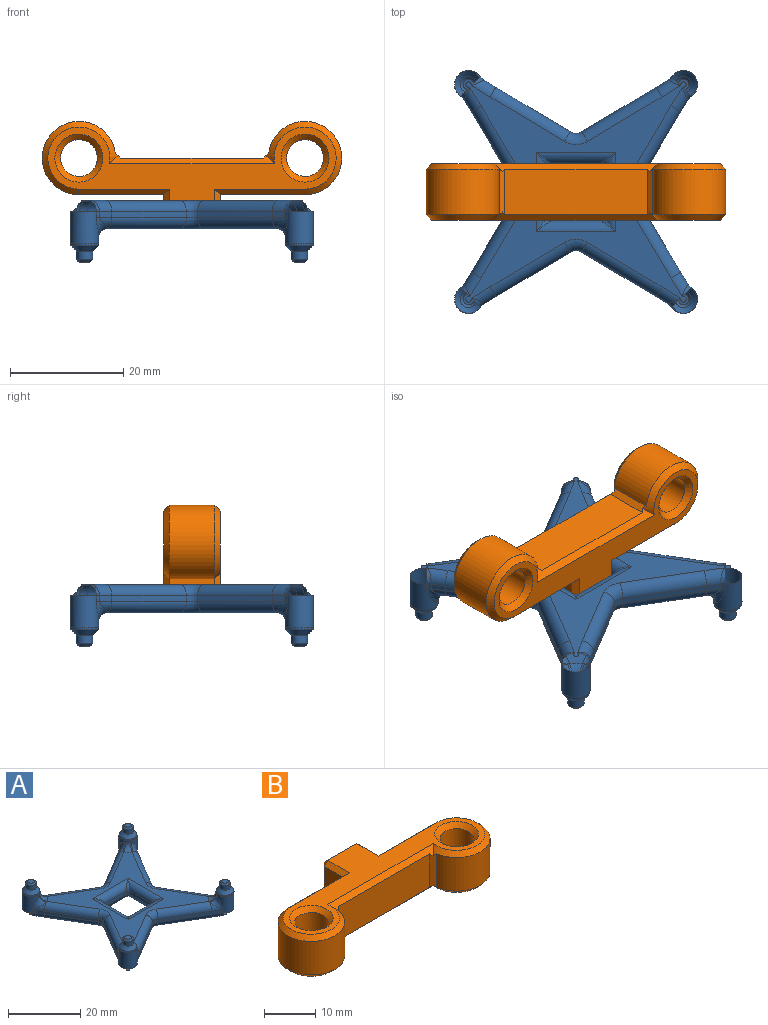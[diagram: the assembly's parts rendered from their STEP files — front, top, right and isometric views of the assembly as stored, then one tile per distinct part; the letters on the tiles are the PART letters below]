
ASSEMBLY  parts=2 mates=1
PART A: 150 faces, bbox 45x45x13 mm
  f0: plane 33.47x33.47mm, normal (0,0,1), area 377.1mm2, adj f40,f41,f42,f53,f54,f57,f58,f59
  f1: plane 41x41mm, normal (0,0,-1), area 402.7mm2, adj f44,f45,f46,f49,f50,f55,f56,f60
  f2: cylinder r=2.5mm len=5.56mm, axis (0,0,-1), area 58.7mm2, adj f73,f138,f139,f140,f142,f143,f144,f145
  f3: cylinder r=1.45mm len=2.9mm, axis (0,0,-1), area 13.7mm2, adj f17,f109
  f4: plane 1.9x1.9mm, normal (0,0,1), area 2.8mm2, adj f17
  f5: cylinder r=2.5mm len=5.56mm, axis (0,0,-1), area 58.7mm2, adj f74,f120,f121,f122,f123,f125,f126,f127
  f6: cylinder r=1.45mm len=2.9mm, axis (0,0,-1), area 13.7mm2, adj f16,f106
  f7: plane 1.9x1.9mm, normal (0,0,1), area 2.8mm2, adj f16
  f8: cylinder r=2.5mm len=5.56mm, axis (0,0,-1), area 58.7mm2, adj f56,f111,f112,f113,f115,f116,f117,f118
  f9: cylinder r=1.45mm len=2.9mm, axis (0,0,-1), area 13.7mm2, adj f15,f107
  f10: plane 1.9x1.9mm, normal (0,0,1), area 2.8mm2, adj f15
  f11: cylinder r=2.5mm len=5.56mm, axis (0,0,-1), area 58.7mm2, adj f55,f129,f130,f131,f133,f134,f135,f136
  f12: cylinder r=1.45mm len=2.9mm, axis (0,0,-1), area 13.7mm2, adj f14,f108
  f13: plane 1.9x1.9mm, normal (0,0,1), area 2.8mm2, adj f14
  f14: cone r=0.95mm half-angle=45deg, axis (0,0,-1), area 5.3mm2, adj f12,f13
  f15: cone r=0.95mm half-angle=45deg, axis (0,0,-1), area 5.3mm2, adj f9,f10
  f16: cone r=0.95mm half-angle=45deg, axis (0,0,-1), area 5.3mm2, adj f6,f7
  f17: cone r=0.95mm half-angle=45deg, axis (0,0,-1), area 5.3mm2, adj f3,f4
  f18: plane 8.6x1mm, normal (0,-1,0), area 8.6mm2, adj f89,f90,f101,f104
  f19: plane 8.6x1mm, normal (1,0,0), area 8.6mm2, adj f87,f91,f98,f104
  f20: plane 8.6x1mm, normal (0,1,0), area 8.6mm2, adj f86,f93,f95,f98
  f21: plane 8.6x1mm, normal (-1,0,0), area 8.6mm2, adj f88,f92,f95,f101
  f22: plane 13.15x7.85mm, normal (0.51,0.86,0), area 15.3mm2, adj f30,f77,f81,f84
  f23: plane 13.15x7.85mm, normal (-0.51,0.86,0), area 15.3mm2, adj f31,f78,f81,f82
  f24: plane 13.15x7.85mm, normal (0.86,-0.51,0), area 15.3mm2, adj f32,f58,f66,f70
  f25: plane 13.15x7.85mm, normal (0.86,0.51,0), area 15.3mm2, adj f33,f57,f65,f66
  f26: plane 13.15x7.85mm, normal (-0.86,-0.51,0), area 15.3mm2, adj f37,f53,f63,f69
  f27: plane 13.15x7.85mm, normal (-0.86,0.51,0), area 15.3mm2, adj f36,f54,f63,f64
  f28: plane 13.15x7.85mm, normal (-0.51,-0.86,0), area 15.3mm2, adj f34,f41,f43,f46
  f29: plane 13.15x7.85mm, normal (0.51,-0.86,0), area 15.3mm2, adj f35,f40,f43,f45
  f30: plane 2.17x1.35mm, normal (0.53,0.85,0), area 2.6mm2, adj f22,f75,f85,f138
  f31: plane 2.17x1.35mm, normal (-0.53,0.85,0), area 2.6mm2, adj f23,f76,f80,f120
  f32: plane 2.17x1.35mm, normal (0.85,-0.53,0), area 2.6mm2, adj f24,f52,f72,f126
  f33: plane 2.17x1.35mm, normal (0.85,0.53,0), area 2.6mm2, adj f25,f51,f61,f116
  f34: plane 2.17x1.35mm, normal (-0.53,-0.85,0), area 2.6mm2, adj f28,f39,f50,f111
  f35: plane 2.17x1.35mm, normal (0.53,-0.85,0), area 2.6mm2, adj f29,f38,f49,f134
  f36: plane 2.17x1.35mm, normal (-0.85,0.53,0), area 2.6mm2, adj f27,f48,f60,f129
  f37: plane 2.17x1.35mm, normal (-0.85,-0.53,0), area 2.6mm2, adj f26,f47,f71,f143
  f38: cylinder r=2mm len=2.98mm, axis (-0.85,-0.53,0), area 3.5mm2, adj f35,f40,f135,f136
  f39: cylinder r=2mm len=2.98mm, axis (0.85,-0.53,0), area 3.5mm2, adj f34,f41,f112,f113
  f40: cylinder r=2mm len=14.19mm, axis (0.86,0.51,0), area 48.1mm2, adj f0,f29,f38,f42,f135
  f41: cylinder r=2mm len=14.19mm, axis (0.86,-0.51,0), area 48.1mm2, adj f0,f28,f39,f42,f113
  f42: torus R=4mm, axis (0,0,1), area 9.2mm2, adj f0,f40,f41,f43
  f43: cylinder r=2mm len=2.05mm, axis (0,0,-1), area 2.2mm2, adj f28,f29,f42,f44
  f44: torus R=4mm, axis (0,0,1), area 9.2mm2, adj f1,f43,f45,f46
  f45: cylinder r=2mm len=14.19mm, axis (-0.86,-0.51,0), area 48.1mm2, adj f1,f29,f44,f49
  f46: cylinder r=2mm len=14.19mm, axis (-0.86,0.51,0), area 48.1mm2, adj f1,f28,f44,f50
  f47: cylinder r=2mm len=2.98mm, axis (0.53,-0.85,0), area 3.5mm2, adj f37,f53,f144,f145
  f48: cylinder r=2mm len=2.98mm, axis (0.53,0.85,0), area 3.5mm2, adj f36,f54,f130,f131
  f49: cylinder r=2mm len=4.36mm, axis (-0.85,-0.53,0), area 10.1mm2, adj f1,f35,f45,f132
  f50: cylinder r=2mm len=4.36mm, axis (0.85,-0.53,0), area 10.1mm2, adj f1,f34,f46,f110
  f51: cylinder r=2mm len=2.98mm, axis (0.53,-0.85,0), area 3.5mm2, adj f33,f57,f117,f118
  f52: cylinder r=2mm len=2.98mm, axis (0.53,0.85,0), area 3.5mm2, adj f32,f58,f125,f127
  f53: cylinder r=2mm len=14.19mm, axis (0.51,-0.86,0), area 48.1mm2, adj f0,f26,f47,f59,f144
  f54: cylinder r=2mm len=14.19mm, axis (-0.51,-0.86,0), area 48.1mm2, adj f0,f27,f48,f59,f131
  f55: torus R=0.5mm, axis (0,0,1), area 20.5mm2, adj f1,f11,f128,f132
  f56: torus R=0.5mm, axis (0,0,1), area 20.5mm2, adj f1,f8,f110,f114
  f57: cylinder r=2mm len=14.19mm, axis (-0.51,0.86,0), area 48.1mm2, adj f0,f25,f51,f62,f117
  f58: cylinder r=2mm len=14.19mm, axis (0.51,0.86,0), area 48.1mm2, adj f0,f24,f52,f62,f125
  f59: torus R=4mm, axis (0,0,1), area 9.2mm2, adj f0,f53,f54,f63
  f60: cylinder r=2mm len=4.36mm, axis (0.53,0.85,0), area 10.1mm2, adj f1,f36,f64,f128
  f61: cylinder r=2mm len=4.36mm, axis (0.53,-0.85,0), area 10.1mm2, adj f1,f33,f65,f114
  f62: torus R=4mm, axis (0,0,1), area 9.2mm2, adj f0,f57,f58,f66
  f63: cylinder r=2mm len=2.05mm, axis (0,0,1), area 2.2mm2, adj f26,f27,f59,f67
  f64: cylinder r=2mm len=14.19mm, axis (0.51,0.86,0), area 48.1mm2, adj f1,f27,f60,f67
  f65: cylinder r=2mm len=14.19mm, axis (0.51,-0.86,0), area 48.1mm2, adj f1,f25,f61,f68
  f66: cylinder r=2mm len=2.05mm, axis (0,0,-1), area 2.2mm2, adj f24,f25,f62,f68
  f67: torus R=4mm, axis (0,0,1), area 9.2mm2, adj f1,f63,f64,f69
  f68: torus R=4mm, axis (0,0,1), area 9.2mm2, adj f1,f65,f66,f70
  f69: cylinder r=2mm len=14.19mm, axis (-0.51,0.86,0), area 48.1mm2, adj f1,f26,f67,f71
  f70: cylinder r=2mm len=14.19mm, axis (-0.51,-0.86,0), area 48.1mm2, adj f1,f24,f68,f72
  f71: cylinder r=2mm len=4.36mm, axis (0.53,-0.85,0), area 10.1mm2, adj f1,f37,f69,f141
  f72: cylinder r=2mm len=4.36mm, axis (0.53,0.85,0), area 10.1mm2, adj f1,f32,f70,f124
  f73: torus R=0.5mm, axis (0,0,1), area 20.5mm2, adj f1,f2,f137,f141
  f74: torus R=0.5mm, axis (0,0,1), area 20.5mm2, adj f1,f5,f119,f124
  f75: cylinder r=2mm len=4.36mm, axis (0.85,-0.53,0), area 10.1mm2, adj f1,f30,f77,f137
  f76: cylinder r=2mm len=4.36mm, axis (-0.85,-0.53,0), area 10.1mm2, adj f1,f31,f78,f119
  f77: cylinder r=2mm len=14.19mm, axis (0.86,-0.51,0), area 48.1mm2, adj f1,f22,f75,f79
  f78: cylinder r=2mm len=14.19mm, axis (0.86,0.51,0), area 48.1mm2, adj f1,f23,f76,f79
  f79: torus R=4mm, axis (0,0,1), area 9.2mm2, adj f1,f77,f78,f81
  f80: cylinder r=2mm len=2.98mm, axis (-0.85,-0.53,0), area 3.5mm2, adj f31,f82,f121,f122
  f81: cylinder r=2mm len=2.05mm, axis (0,0,1), area 2.2mm2, adj f22,f23,f79,f83
  f82: cylinder r=2mm len=14.19mm, axis (-0.86,-0.51,0), area 48.1mm2, adj f0,f23,f80,f83,f122
  f83: torus R=4mm, axis (0,0,1), area 9.2mm2, adj f0,f81,f82,f84
  f84: cylinder r=2mm len=14.19mm, axis (-0.86,0.51,0), area 48.1mm2, adj f0,f22,f83,f85,f140
  f85: cylinder r=2mm len=2.98mm, axis (0.85,-0.53,0), area 3.5mm2, adj f30,f84,f139,f140
  f86: cylinder r=2mm len=14mm, axis (1,0,0), area 35.5mm2, adj f1,f20,f96,f99
  f87: cylinder r=2mm len=14mm, axis (0,-1,0), area 35.5mm2, adj f1,f19,f99,f105
  f88: cylinder r=2mm len=14mm, axis (0,1,0), area 35.5mm2, adj f1,f21,f96,f102
  f89: cylinder r=2mm len=14mm, axis (-1,0,0), area 35.5mm2, adj f1,f18,f102,f105
  f90: cylinder r=2mm len=14mm, axis (1,0,0), area 35.5mm2, adj f0,f18,f100,f103
  f91: cylinder r=2mm len=14mm, axis (0,1,0), area 35.5mm2, adj f0,f19,f97,f103
  f92: cylinder r=2mm len=14mm, axis (0,-1,0), area 35.5mm2, adj f0,f21,f94,f100
  f93: cylinder r=2mm len=14mm, axis (-1,0,0), area 35.5mm2, adj f0,f20,f94,f97
  f94: bspline ~2.7x2.7mm, area 1.5mm2, adj f92,f93,f95
  f95: plane 1x0.7mm, normal (-0.71,0.71,0), area 1mm2, adj f20,f21,f94,f96
  f96: bspline ~2.7x2.7mm, area 1.5mm2, adj f86,f88,f95
  f97: bspline ~2.7x2.7mm, area 1.5mm2, adj f91,f93,f98
  f98: plane 1x0.7mm, normal (0.71,0.71,0), area 1mm2, adj f19,f20,f97,f99
  f99: bspline ~2.7x2.7mm, area 1.5mm2, adj f86,f87,f98
  f100: bspline ~2.7x2.7mm, area 1.5mm2, adj f90,f92,f101
  f101: plane 1x0.7mm, normal (-0.71,-0.71,0), area 1mm2, adj f18,f21,f100,f102
  f102: bspline ~2.7x2.7mm, area 1.5mm2, adj f88,f89,f101
  f103: bspline ~2.7x2.7mm, area 1.5mm2, adj f90,f91,f104
  f104: plane 1x0.7mm, normal (0.71,-0.71,0), area 1mm2, adj f18,f19,f103,f105
  f105: bspline ~2.7x2.7mm, area 1.5mm2, adj f87,f89,f104
  f106: cone r=1.45mm half-angle=45deg, axis (0,0,-1), area 17.3mm2, adj f6,f148
  f107: cone r=1.45mm half-angle=45deg, axis (0,0,-1), area 17.3mm2, adj f9,f147
  f108: cone r=1.45mm half-angle=45deg, axis (0,0,-1), area 17.3mm2, adj f12,f146
  f109: cone r=1.45mm half-angle=45deg, axis (0,0,-1), area 17.3mm2, adj f3,f149
  f110: bspline ~2.44x2.17mm, area 1.2mm2, adj f50,f56,f111
  f111: cylinder r=2mm len=1mm, axis (0,0,-1), area 0.8mm2, adj f8,f34,f110,f112
  f112: bspline ~4.37x3.42mm, area 6.9mm2, adj f8,f39,f111,f113
  f113: bspline ~2.08x1.97mm, area 1.3mm2, adj f8,f39,f41,f112,f115
  f114: bspline ~2.17x2mm, area 1.2mm2, adj f56,f61,f116
  f115: torus R=4.5mm, axis (0,0,1), area 5.2mm2, adj f0,f8,f113,f117
  f116: cylinder r=2mm len=1mm, axis (0,0,-1), area 0.8mm2, adj f8,f33,f114,f118
  f117: bspline ~2.08x1.97mm, area 1.3mm2, adj f8,f51,f57,f115,f118
  f118: bspline ~4.37x3.42mm, area 6.9mm2, adj f8,f51,f116,f117
  f119: bspline ~2.17x2mm, area 1.2mm2, adj f74,f76,f120
  f120: cylinder r=2mm len=1mm, axis (0,0,-1), area 0.8mm2, adj f5,f31,f119,f121
  f121: bspline ~4.37x3.42mm, area 6.9mm2, adj f5,f80,f120,f122
  f122: bspline ~2.08x1.97mm, area 1.3mm2, adj f5,f80,f82,f121,f123
  f123: torus R=4.5mm, axis (0,0,1), area 5.2mm2, adj f0,f5,f122,f125
  f124: bspline ~2.17x2mm, area 1.2mm2, adj f72,f74,f126
  f125: bspline ~2.08x1.97mm, area 1.3mm2, adj f5,f52,f58,f123,f127
  f126: cylinder r=2mm len=1mm, axis (0,0,-1), area 0.8mm2, adj f5,f32,f124,f127
  f127: bspline ~4.37x3.42mm, area 6.9mm2, adj f5,f52,f125,f126
  f128: bspline ~2.17x2mm, area 1.2mm2, adj f55,f60,f129
  f129: cylinder r=2mm len=1mm, axis (0,0,-1), area 0.8mm2, adj f11,f36,f128,f130
  f130: bspline ~4.37x3.42mm, area 6.9mm2, adj f11,f48,f129,f131
  f131: bspline ~2.08x1.97mm, area 1.3mm2, adj f11,f48,f54,f130,f133
  f132: bspline ~2.17x2mm, area 1.2mm2, adj f49,f55,f134
  f133: torus R=4.5mm, axis (0,0,1), area 5.2mm2, adj f0,f11,f131,f135
  f134: cylinder r=2mm len=1mm, axis (0,0,-1), area 0.8mm2, adj f11,f35,f132,f136
  f135: bspline ~2.08x1.97mm, area 1.3mm2, adj f11,f38,f40,f133,f136
  f136: bspline ~4.37x3.42mm, area 6.9mm2, adj f11,f38,f134,f135
  f137: bspline ~2.44x2.17mm, area 1.2mm2, adj f73,f75,f138
  f138: cylinder r=2mm len=1mm, axis (0,0,-1), area 0.8mm2, adj f2,f30,f137,f139
  f139: bspline ~4.37x3.42mm, area 6.9mm2, adj f2,f85,f138,f140
  f140: bspline ~2.08x1.97mm, area 1.3mm2, adj f2,f84,f85,f139,f142
  f141: bspline ~2.17x2mm, area 1.2mm2, adj f71,f73,f143
  f142: torus R=4.5mm, axis (0,0,1), area 5.2mm2, adj f0,f2,f140,f144
  f143: cylinder r=2mm len=1mm, axis (0,0,-1), area 0.8mm2, adj f2,f37,f141,f145
  f144: bspline ~2.08x1.97mm, area 1.3mm2, adj f2,f47,f53,f142,f145
  f145: bspline ~4.37x3.42mm, area 6.9mm2, adj f2,f47,f143,f144
  f146: torus R=0.5mm, axis (0,0,1), area 7mm2, adj f11,f108
  f147: torus R=0.5mm, axis (0,0,1), area 7mm2, adj f8,f107
  f148: torus R=0.5mm, axis (0,0,1), area 7mm2, adj f5,f106
  f149: torus R=0.5mm, axis (0,0,1), area 7mm2, adj f2,f109
PART B: 40 faces, bbox 53.9x19.5x10 mm
  f0: plane 8x8mm, normal (0,1,0), area 64mm2, adj f20,f28,f29,f33
  f1: plane 8x5mm, normal (-1,0,0), area 40mm2, adj f2,f19,f20,f21
  f2: plane 15x8mm, normal (0,1,0), area 120mm2, adj f1,f3,f15,f16
  f3: cylinder r=6.5mm len=13mm, axis (0,0,-1), area 238.1mm2, adj f2,f12,f13,f38
  f4: plane 25.13x8mm, normal (0,-1,0), area 201.1mm2, adj f14,f17,f38,f39
  f5: cylinder r=6.5mm len=13mm, axis (0,0,-1), area 238.1mm2, adj f6,f18,f22,f39
  f6: plane 15x8mm, normal (0,1,0), area 120mm2, adj f5,f8,f23,f26
  f7: cylinder r=3.25mm len=8mm, axis (0,0,-1), area 163.4mm2, adj f35,f37
  f8: plane 8x5mm, normal (1,0,0), area 40mm2, adj f6,f27,f30,f33
  f9: cylinder r=3.25mm len=8mm, axis (0,0,-1), area 163.4mm2, adj f34,f36
  f10: plane 51x17mm, normal (0,0,1), area 268mm2, adj f12,f14,f15,f18,f19,f23,f27,f28
  f11: plane 51x17mm, normal (0,0,-1), area 268mm2, adj f13,f16,f17,f21,f22,f26,f29,f30
  f12: cone r=5.5mm half-angle=45deg, axis (0,0,-1), area 41mm2, adj f3,f10,f14,f15,f38
  f13: cone r=6.5mm half-angle=45deg, axis (0,0,1), area 41mm2, adj f3,f11,f16,f17,f38
  f14: plane 29.19x1.44mm, normal (0,-0.71,0.71), area 40.3mm2, adj f4,f10,f12,f18,f38,f39
  f15: plane 16x1mm, normal (0,0.71,0.71), area 21.9mm2, adj f2,f10,f12,f19
  f16: plane 16x1mm, normal (0,0.71,-0.71), area 21.9mm2, adj f2,f11,f13,f21
  f17: plane 29.19x1.44mm, normal (0,-0.71,-0.71), area 40.3mm2, adj f4,f11,f13,f22,f38,f39
  f18: cone r=5.5mm half-angle=45deg, axis (0,0,-1), area 41mm2, adj f5,f10,f14,f23,f39
  f19: plane 6x1mm, normal (-0.71,0,0.71), area 7.8mm2, adj f1,f10,f15,f24
  f20: plane 8x1mm, normal (-0.71,0.71,0), area 11.3mm2, adj f0,f1,f24,f25
  f21: plane 6x1mm, normal (-0.71,0,-0.71), area 7.8mm2, adj f1,f11,f16,f25
  f22: cone r=6.5mm half-angle=45deg, axis (0,0,1), area 41mm2, adj f5,f11,f17,f26,f39
  f23: plane 16x1mm, normal (0,0.71,0.71), area 21.9mm2, adj f6,f10,f18,f27
  f24: plane 1x1mm, normal (-0.58,0.58,0.58), area 0.9mm2, adj f19,f20,f28
  f25: plane 1x1mm, normal (-0.58,0.58,-0.58), area 0.9mm2, adj f20,f21,f29
  f26: plane 16x1mm, normal (0,0.71,-0.71), area 21.9mm2, adj f6,f11,f22,f30
  f27: plane 6x1mm, normal (0.71,0,0.71), area 7.8mm2, adj f8,f10,f23,f31
  f28: plane 8x1mm, normal (0,0.71,0.71), area 11.3mm2, adj f0,f10,f24,f31
  f29: plane 8x1mm, normal (0,0.71,-0.71), area 11.3mm2, adj f0,f11,f25,f32
  f30: plane 6x1mm, normal (0.71,0,-0.71), area 7.8mm2, adj f8,f11,f26,f32
  f31: plane 1x1mm, normal (0.58,0.58,0.58), area 0.9mm2, adj f27,f28,f33
  f32: plane 1x1mm, normal (0.58,0.58,-0.58), area 0.9mm2, adj f29,f30,f33
  f33: plane 8x1mm, normal (0.71,0.71,0), area 11.3mm2, adj f0,f8,f31,f32
  f34: cone r=4.25mm half-angle=45deg, axis (0,0,-1), area 33.3mm2, adj f9,f11
  f35: cone r=4.25mm half-angle=45deg, axis (0,0,-1), area 33.3mm2, adj f7,f11
  f36: cone r=3.25mm half-angle=45deg, axis (0,0,1), area 33.3mm2, adj f9,f10
  f37: cone r=3.25mm half-angle=45deg, axis (0,0,1), area 33.3mm2, adj f7,f10
  f38: plane 8.02x1.01mm, normal (0.66,-0.75,0), area 10mm2, adj f3,f4,f12,f13,f14,f17
  f39: plane 8.02x1.01mm, normal (-0.66,-0.75,0), area 10mm2, adj f4,f5,f14,f17,f18,f22
PLACE A rot(axis=(0,1,0),180deg) t=(-1.81,0,-18.34)mm
PLACE B rot(axis=(-1,0,0),90deg) t=(-1.81,-5,34.16)mm
MATE fastened B.f0 <-> A.f0  axis (0,0,-1) through (-1.81,0,-18.34)mm
